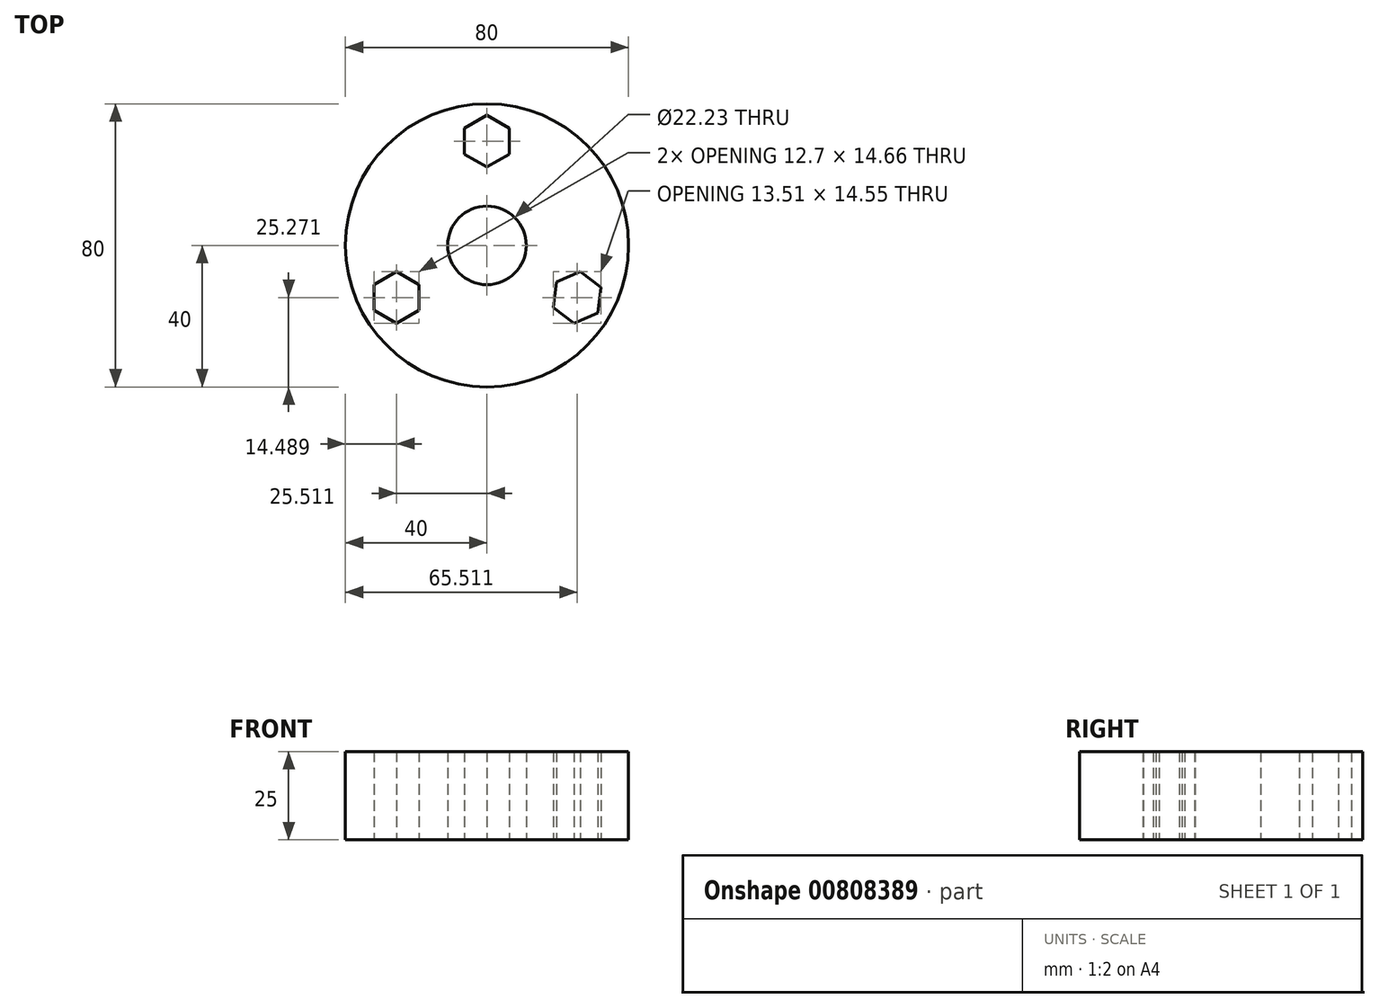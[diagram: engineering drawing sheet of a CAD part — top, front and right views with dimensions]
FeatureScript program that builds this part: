
annotation { "Feature Type Name" : "Feature", "Feature Type Description" : "" }
export const myFeature = defineFeature(function(context is Context, id is Id, definition is map)
    precondition{}
    {
        {
            var Q0;
            Q0=qCreatedBy(makeId("Top.planeOp"),FACE);
            var sketch = newSketch(context, id + "F0", { "sketchPlane" : qUnion([Q0])});
            skCircle(sketch, "E0", {"center": v(0, 0) * mm, "radius": 40 * mm});
            skCircle(sketch, "E1", {"center": v(0, 0) * mm, "radius": 11.11 * mm});
            skCircle(sketch, "E2.cCircle", {"center": v(0, 29.46) * mm, "radius": 6.35 * mm, "construction": true});
            skLineSegment(sketch, "E2.0", {"start": v(6.35, 33.12) * mm, "end": v(6.35, 25.8) * mm});
            skLineSegment(sketch, "E2.1", {"start": v(6.35, 25.8) * mm, "end": v(0, 22.12) * mm});
            skLineSegment(sketch, "E2.2", {"start": v(0, 22.12) * mm, "end": v(-6.35, 25.8) * mm});
            skLineSegment(sketch, "E2.3", {"start": v(-6.35, 25.8) * mm, "end": v(-6.35, 33.12) * mm});
            skLineSegment(sketch, "E2.4", {"start": v(-6.35, 33.12) * mm, "end": v(0, 36.79) * mm});
            skLineSegment(sketch, "E2.5", {"start": v(0, 36.79) * mm, "end": v(6.35, 33.12) * mm});
            skPoint(sketch, "E2.0.midPoint", {"position": v(6.35, 29.46) * mm});
            skCircle(sketch, "E3.1.0", {"center": v(-25.51, -14.73) * mm, "radius": 6.35 * mm, "construction": true});
            skCircle(sketch, "E3.2.0", {"center": v(25.51, -14.73) * mm, "radius": 6.35 * mm, "construction": true});
            skLineSegment(sketch, "E4.0", {"start": v(-19.16, -11.06) * mm, "end": v(-19.16, -18.4) * mm});
            skLineSegment(sketch, "E4.1", {"start": v(-19.16, -18.4) * mm, "end": v(-25.51, -22.06) * mm});
            skLineSegment(sketch, "E4.2", {"start": v(-25.51, -22.06) * mm, "end": v(-31.86, -18.4) * mm});
            skLineSegment(sketch, "E4.3", {"start": v(-31.86, -18.4) * mm, "end": v(-31.86, -11.06) * mm});
            skLineSegment(sketch, "E4.4", {"start": v(-31.86, -11.06) * mm, "end": v(-25.51, -7.4) * mm});
            skLineSegment(sketch, "E4.5", {"start": v(-25.51, -7.4) * mm, "end": v(-19.16, -11.06) * mm});
            skPoint(sketch, "E4.0.midPoint", {"position": v(-19.16, -14.73) * mm});
            skLineSegment(sketch, "E5.0", {"start": v(32.27, -11.88) * mm, "end": v(31.36, -19.16) * mm});
            skLineSegment(sketch, "E5.1", {"start": v(31.36, -19.16) * mm, "end": v(24.6, -22) * mm});
            skLineSegment(sketch, "E5.2", {"start": v(24.6, -22) * mm, "end": v(18.75, -17.58) * mm});
            skLineSegment(sketch, "E5.3", {"start": v(18.75, -17.58) * mm, "end": v(19.67, -10.3) * mm});
            skLineSegment(sketch, "E5.4", {"start": v(19.67, -10.3) * mm, "end": v(26.42, -7.45) * mm});
            skLineSegment(sketch, "E5.5", {"start": v(26.42, -7.45) * mm, "end": v(32.27, -11.88) * mm});
            skPoint(sketch, "E5.0.midPoint", {"position": v(31.81, -15.52) * mm});
            skSolve(sketch);
        }
        {
            var Q0;
            Q0=makeQuery(id+"F0.imprint","IMPRINT",FACE,{"disambiguationData":[TD([[makeQuery(id+"F0.imprint","IMPRINT",EDGE,{"derivedFrom":sQuery(id+"F0.wireOp",EDGE,"E0")}),1.0]])]});
            extrude(context, id + "F1", {"entities" : qUnion([Q0]), "depth" : 7.5 * mm, "offsetDistance" : 25 * mm});
        }
        {
            var Q0;
            Q0 = qSketchRegion(id + "F0", true);
            extrude(context, id + "F2", {"entities" : qUnion([Q0]), "operationType" : NewBodyOperationType.ADD, "depth" : 25 * mm, "offsetDistance" : 25 * mm});
        }
    });
